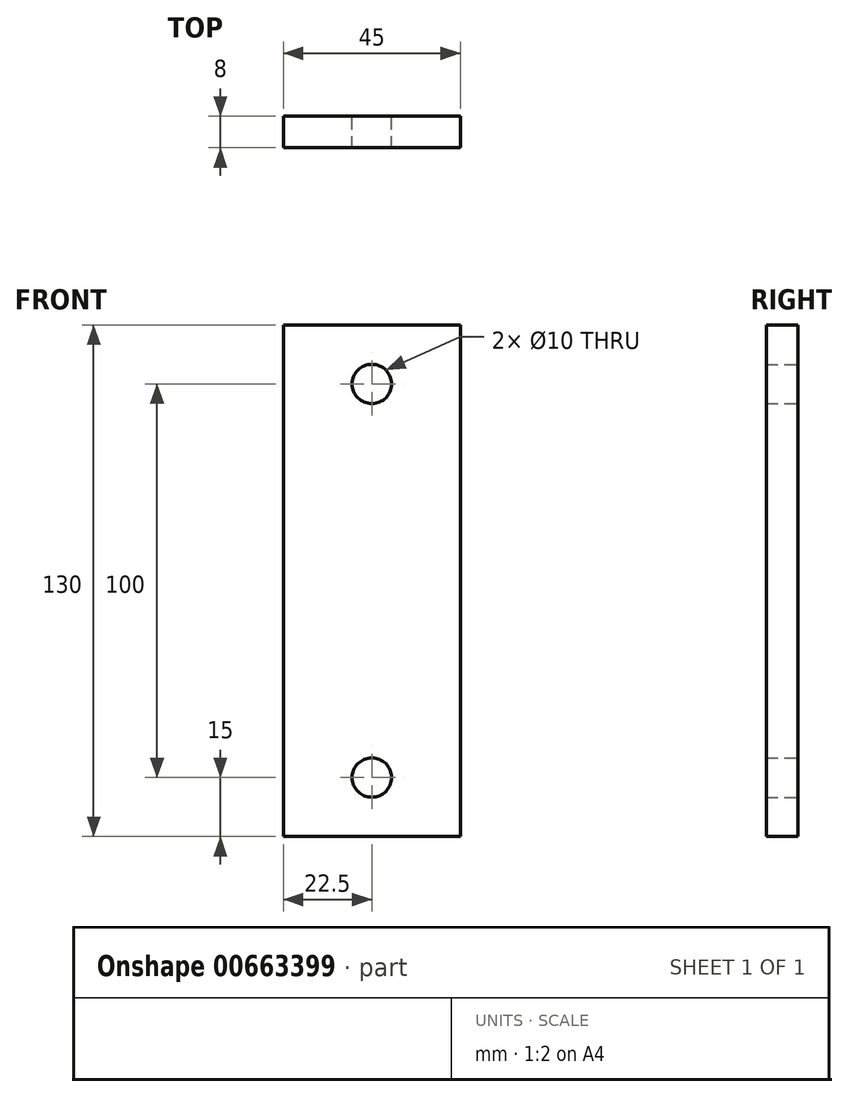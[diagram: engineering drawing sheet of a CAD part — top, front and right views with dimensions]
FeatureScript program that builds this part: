
annotation { "Feature Type Name" : "Feature", "Feature Type Description" : "" }
export const myFeature = defineFeature(function(context is Context, id is Id, definition is map)
    precondition{}
    {
        {
            var Q0;
            Q0=qCreatedBy(makeId("Front.planeOp"),FACE);
            var sketch = newSketch(context, id + "F0", { "sketchPlane" : qUnion([Q0])});
            skLineSegment(sketch, "E0.bottom", {"start": v(22.5, 65) * mm, "end": v(-22.5, 65) * mm});
            skLineSegment(sketch, "E0.top", {"start": v(22.5, -65) * mm, "end": v(-22.5, -65) * mm});
            skLineSegment(sketch, "E0.left", {"start": v(22.5, 65) * mm, "end": v(22.5, -65) * mm});
            skLineSegment(sketch, "E0.right", {"start": v(-22.5, 65) * mm, "end": v(-22.5, -65) * mm});
            skPoint(sketch, "E0.middle", {"position": v(0, 0) * mm});
            skCircle(sketch, "E1", {"center": v(0, -50) * mm, "radius": 5 * mm});
            skCircle(sketch, "E2", {"center": v(0, 50) * mm, "radius": 5 * mm});
            skSolve(sketch);
        }
        {
            var Q0;
            Q0=makeQuery(id+"F0.imprint","IMPRINT",FACE,{"disambiguationData":[TD([[makeQuery(id+"F0.imprint","IMPRINT",EDGE,{"derivedFrom":sQuery(id+"F0.wireOp",EDGE,"E0.bottom")}),1.0]])]});
            extrude(context, id + "F1", {"entities" : qUnion([Q0]), "endBound" : BoundingType.SYMMETRIC, "depth" : 8 * mm, "offsetDistance" : 25 * mm});
        }
    });
